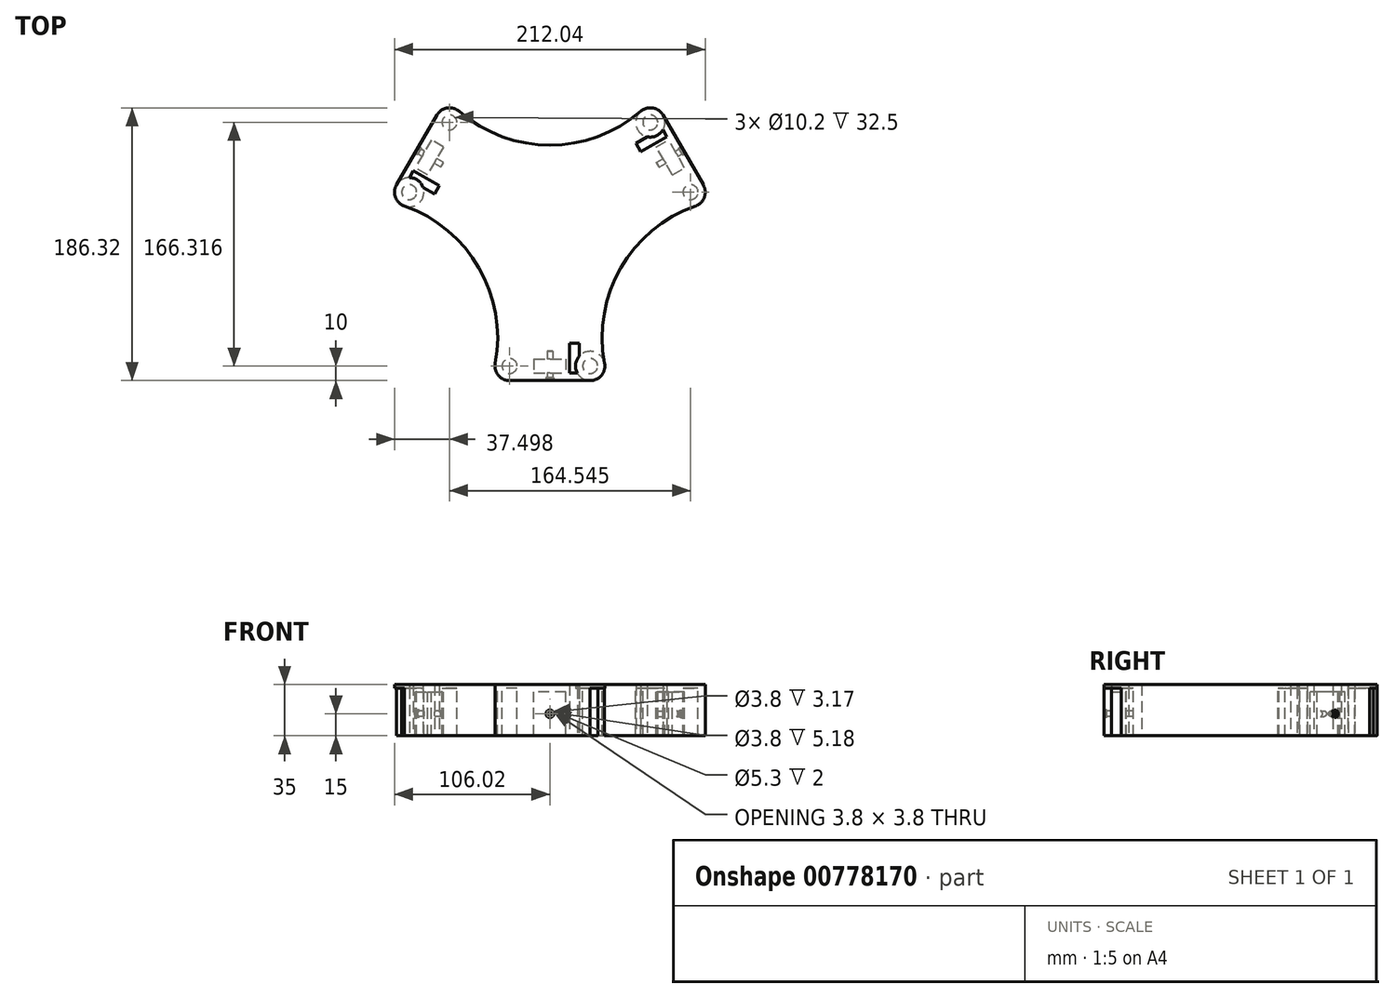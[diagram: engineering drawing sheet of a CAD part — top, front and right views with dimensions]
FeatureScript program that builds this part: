
annotation { "Feature Type Name" : "Feature", "Feature Type Description" : "" }
export const myFeature = defineFeature(function(context is Context, id is Id, definition is map)
    precondition{}
    {
        {
            var Q0;
            Q0=qCreatedBy(makeId("Top.planeOp"),FACE);
            var sketch = newSketch(context, id + "F0", { "sketchPlane" : qUnion([Q0])});
            skCircle(sketch, "E0", {"center": v(0, 0) * mm, "radius": 57.15 * mm, "construction": true});
            skLineSegment(sketch, "E1.bottom", {"start": v(110, 110) * mm, "end": v(-110, 110) * mm, "construction": true});
            skLineSegment(sketch, "E1.top", {"start": v(110, -110) * mm, "end": v(-110, -110) * mm, "construction": true});
            skLineSegment(sketch, "E1.left", {"start": v(110, 110) * mm, "end": v(110, -110) * mm, "construction": true});
            skLineSegment(sketch, "E1.right", {"start": v(-110, 110) * mm, "end": v(-110, -110) * mm, "construction": true});
            skLineSegment(sketch, "E2", {"start": v(0, 0) * mm, "end": v(0, -95) * mm});
            skLineSegment(sketch, "E3", {"start": v(0, 0) * mm, "end": v(-59.96, -34.62) * mm});
            skLineSegment(sketch, "E4", {"start": v(0, 0) * mm, "end": v(-61.29, 35.38) * mm});
            skLineSegment(sketch, "E5.MirrorCS", {"start": v(0, 0) * mm, "end": v(59.96, -34.62) * mm});
            skLineSegment(sketch, "E6.MirrorCS", {"start": v(0, 0) * mm, "end": v(61.29, 35.38) * mm});
            skCircle(sketch, "E7", {"center": v(-27.5, -95) * mm, "radius": 5.1 * mm});
            skCircle(sketch, "E8", {"center": v(-27.5, -95) * mm, "radius": 10 * mm});
            skCircle(sketch, "E9.MirrorC", {"center": v(27.5, -95) * mm, "radius": 10 * mm});
            skCircle(sketch, "E10.MirrorC", {"center": v(27.5, -95) * mm, "radius": 5.1 * mm});
            skLineSegment(sketch, "E11", {"start": v(-27.5, -105) * mm, "end": v(27.5, -105) * mm});
            skCircle(sketch, "E12.1.0", {"center": v(96.02, 23.68) * mm, "radius": 5.1 * mm});
            skCircle(sketch, "E12.1.1", {"center": v(96.02, 23.68) * mm, "radius": 10 * mm});
            skLineSegment(sketch, "E12.1.2", {"start": v(104.68, 28.68) * mm, "end": v(77.18, 76.32) * mm});
            skCircle(sketch, "E12.1.3", {"center": v(68.52, 71.32) * mm, "radius": 10 * mm});
            skCircle(sketch, "E12.1.4", {"center": v(68.52, 71.32) * mm, "radius": 5.1 * mm});
            skCircle(sketch, "E12.2.0", {"center": v(-68.52, 71.32) * mm, "radius": 5.1 * mm});
            skCircle(sketch, "E12.2.1", {"center": v(-68.52, 71.32) * mm, "radius": 10 * mm});
            skLineSegment(sketch, "E12.2.2", {"start": v(-77.18, 76.32) * mm, "end": v(-104.68, 28.68) * mm});
            skCircle(sketch, "E12.2.3", {"center": v(-96.02, 23.68) * mm, "radius": 10 * mm});
            skCircle(sketch, "E12.2.4", {"center": v(-96.02, 23.68) * mm, "radius": 5.1 * mm});
            skArc(sketch, "E13", {"start": v(99.32, 14.24) * mm, "mid": v(48.39, -27.94) * mm, "end": v(37.32, -93.14) * mm});
            skArc(sketch, "E14.1.0", {"start": v(-62, 78.9) * mm, "mid": v(0, 55.87) * mm, "end": v(62, 78.9) * mm});
            skArc(sketch, "E14.2.0", {"start": v(-37.32, -93.14) * mm, "mid": v(-48.39, -27.94) * mm, "end": v(-99.32, 14.24) * mm});
            skSolve(sketch);
        }
        {
            var Q0;
            {var subQ0=sQuery(id+"F0.wireOp",EDGE,"E11");Q0=makeQuery(id+"F0.imprint","IMPRINT",FACE,{"disambiguationData":[TD([[makeQuery(id+"F0.imprint","IMPRINT",EDGE,{"derivedFrom":subQ0}),1.0]])]});}
            var Q1;
            Q1=makeQuery(id+"F0.imprint","IMPRINT",FACE,{"disambiguationData":[TD([[makeQuery(id+"F0.imprint","IMPRINT",EDGE,{"derivedFrom":sQuery(id+"F0.wireOp",EDGE,"E7")}),-1.0]])]});
            var Q2;
            Q2=makeQuery(id+"F0.imprint","IMPRINT",FACE,{"disambiguationData":[TD([[makeQuery(id+"F0.imprint","IMPRINT",EDGE,{"derivedFrom":sQuery(id+"F0.wireOp",EDGE,"E10.MirrorC")}),1.0]])]});
            extrude(context, id + "F1", {"entities" : qUnion([Q0, Q1, Q2]), "oppositeDirection" : true, "depth" : 35 * mm, "offsetDistance" : 25 * mm});
        }
        {
            var Q0;
            Q0=makeQuery(id+"F1.opExtrude","CAP_FACE",FACE,{"disambiguationData":[OSD([sQuery(id+"F0.wireOp",EDGE,"E3"),sQuery(id+"F0.wireOp",EDGE,"E5.MirrorCS"),sQuery(id+"F0.wireOp",EDGE,"E7"),sQuery(id+"F0.wireOp",EDGE,"E8"),sQuery(id+"F0.wireOp",EDGE,"E9.MirrorC"),sQuery(id+"F0.wireOp",EDGE,"E10.MirrorC"),sQuery(id+"F0.wireOp",EDGE,"E11"),sQuery(id+"F0.wireOp",EDGE,"E13"),sQuery(id+"F0.wireOp",EDGE,"E14.2.0")])],"isStart":true});
            var sketch = newSketch(context, id + "F2", { "sketchPlane" : qUnion([Q0])});
            skLineSegment(sketch, "E15.0", {"start": v(-27.5, -105) * mm, "end": v(27.5, -105) * mm});
            skLineSegment(sketch, "E16.bottom", {"start": v(11, -99.83) * mm, "end": v(-11, -99.83) * mm});
            skLineSegment(sketch, "E16.top", {"start": v(11, -90.18) * mm, "end": v(-11, -90.18) * mm});
            skLineSegment(sketch, "E16.left", {"start": v(11, -99.83) * mm, "end": v(11, -90.18) * mm});
            skLineSegment(sketch, "E16.right", {"start": v(-11, -99.83) * mm, "end": v(-11, -90.18) * mm});
            skPoint(sketch, "E16.middle", {"position": v(0, -95) * mm});
            skPoint(sketch, "E16.middle.positionSnap0", {"position": v(0, -105) * mm});
            skPoint(sketch, "E16.centerSnap0", {"position": v(0, -105) * mm});
            skSolve(sketch);
        }
        {
            var Q0;
            Q0=makeQuery(id+"F2.imprint","IMPRINT",FACE,{"disambiguationData":[TD([[makeQuery(id+"F2.imprint","IMPRINT",EDGE,{"derivedFrom":sQuery(id+"F2.wireOp",EDGE,"E16.bottom")}),-1.0]])]});
            var Q1;
            Q1=makeQuery(id+"F1.opExtrude","CAP_FACE",FACE,{"disambiguationData":[OSD([sQuery(id+"F0.wireOp",EDGE,"E3"),sQuery(id+"F0.wireOp",EDGE,"E5.MirrorCS"),sQuery(id+"F0.wireOp",EDGE,"E7"),sQuery(id+"F0.wireOp",EDGE,"E8"),sQuery(id+"F0.wireOp",EDGE,"E9.MirrorC"),sQuery(id+"F0.wireOp",EDGE,"E10.MirrorC"),sQuery(id+"F0.wireOp",EDGE,"E11"),sQuery(id+"F0.wireOp",EDGE,"E13"),sQuery(id+"F0.wireOp",EDGE,"E14.2.0")])],"isStart":false});
            extrude(context, id + "F3", {"entities" : qUnion([Q0]), "operationType" : NewBodyOperationType.REMOVE, "endBound" : BoundingType.UP_TO_SURFACE, "oppositeDirection" : true, "depth" : 25 * mm, "endBoundEntityFace" : qUnion([Q1]), "offsetDistance" : 25 * mm});
        }
        {
            var Q0;
            Q0=makeQuery(id+"F2.imprint","IMPRINT",FACE,{"disambiguationData":[TD([[makeQuery(id+"F2.imprint","IMPRINT",EDGE,{"derivedFrom":sQuery(id+"F2.wireOp",EDGE,"E16.bottom")}),-1.0]])]});
            extrude(context, id + "F4", {"entities" : qUnion([Q0]), "operationType" : NewBodyOperationType.ADD, "oppositeDirection" : true, "depth" : 5 * mm, "offsetDistance" : 25 * mm});
        }
        {
            var Q0;
            Q0=makeQuery(id+"F0.imprint","IMPRINT",FACE,{"disambiguationData":[TD([[makeQuery(id+"F0.imprint","IMPRINT",EDGE,{"derivedFrom":sQuery(id+"F0.wireOp",EDGE,"E7")}),1.0]])]});
            var Q1;
            Q1=makeQuery(id+"F0.imprint","IMPRINT",FACE,{"disambiguationData":[TD([[makeQuery(id+"F0.imprint","IMPRINT",EDGE,{"derivedFrom":sQuery(id+"F0.wireOp",EDGE,"E10.MirrorC")}),-1.0]])]});
            extrude(context, id + "F5", {"entities" : qUnion([Q0, Q1]), "operationType" : NewBodyOperationType.ADD, "oppositeDirection" : true, "depth" : 2.5 * mm, "offsetDistance" : 25 * mm});
        }
        {
            var Q0;
            Q0=makeQuery(id+"F1.opExtrude","SWEPT_FACE",FACE,{"disambiguationData":[OSD([sQuery(id+"F0.wireOp",EDGE,"E11")])]});
            var sketch = newSketch(context, id + "F6", { "sketchPlane" : qUnion([Q0])});
            skLineSegment(sketch, "E17.0", {"start": v(-27.5, 0) * mm, "end": v(27.5, 0) * mm});
            skLineSegment(sketch, "E18.0", {"start": v(-27.5, -35) * mm, "end": v(27.5, -35) * mm});
            skLineSegment(sketch, "E19", {"start": v(0, 0) * mm, "end": v(0, -35) * mm, "construction": true});
            skPoint(sketch, "E20", {"position": v(0, -17.5) * mm});
            skCircle(sketch, "E21", {"center": v(0, -20) * mm, "radius": 4.15 * mm});
            skCircle(sketch, "E22", {"center": v(0, -20) * mm, "radius": 2.65 * mm});
            skCircle(sketch, "E23", {"center": v(0, -20) * mm, "radius": 1.9 * mm});
            skSolve(sketch);
        }
        {
            var Q0;
            Q0=makeQuery(id+"F6.imprint","IMPRINT",FACE,{"disambiguationData":[TD([[makeQuery(id+"F6.imprint","IMPRINT",EDGE,{"derivedFrom":sQuery(id+"F6.wireOp",EDGE,"E23")}),1.0]])]});
            extrude(context, id + "F7", {"entities" : qUnion([Q0]), "operationType" : NewBodyOperationType.REMOVE, "oppositeDirection" : true, "depth" : 20 * mm, "offsetDistance" : 25 * mm});
        }
        {
            var Q0;
            Q0=makeQuery(id+"F6.imprint","IMPRINT",FACE,{"disambiguationData":[TD([[makeQuery(id+"F6.imprint","IMPRINT",EDGE,{"derivedFrom":sQuery(id+"F6.wireOp",EDGE,"E22")}),1.0]])]});
            extrude(context, id + "F8", {"entities" : qUnion([Q0]), "operationType" : NewBodyOperationType.REMOVE, "oppositeDirection" : true, "depth" : 2 * mm, "offsetDistance" : 25 * mm});
        }
        {
            var Q0;
            Q0=makeQuery(id+"F1.opExtrude","CAP_FACE",FACE,{"disambiguationData":[OSD([sQuery(id+"F0.wireOp",EDGE,"E3"),sQuery(id+"F0.wireOp",EDGE,"E5.MirrorCS"),sQuery(id+"F0.wireOp",EDGE,"E7"),sQuery(id+"F0.wireOp",EDGE,"E8"),sQuery(id+"F0.wireOp",EDGE,"E9.MirrorC"),sQuery(id+"F0.wireOp",EDGE,"E10.MirrorC"),sQuery(id+"F0.wireOp",EDGE,"E11"),sQuery(id+"F0.wireOp",EDGE,"E13"),sQuery(id+"F0.wireOp",EDGE,"E14.2.0")])],"isStart":false});
            var sketch = newSketch(context, id + "F9", { "sketchPlane" : qUnion([Q0])});
            skLineSegment(sketch, "E24.bottom", {"start": v(20.02, 79.43) * mm, "end": v(13.37, 79.43) * mm});
            skLineSegment(sketch, "E24.top", {"start": v(20.02, 99.83) * mm, "end": v(13.37, 99.83) * mm});
            skLineSegment(sketch, "E24.left", {"start": v(20.02, 79.43) * mm, "end": v(20.02, 99.83) * mm});
            skLineSegment(sketch, "E24.right", {"start": v(13.37, 79.43) * mm, "end": v(13.37, 99.83) * mm});
            skPoint(sketch, "E24.middle", {"position": v(16.7, 89.63) * mm});
            skLineSegment(sketch, "E25.0", {"start": v(11, 99.83) * mm, "end": v(11, 90.18) * mm});
            skCircle(sketch, "E26.0", {"center": v(27.5, 95) * mm, "radius": 5.1 * mm});
            skLineSegment(sketch, "E27", {"start": v(11, 95) * mm, "end": v(13.37, 95) * mm});
            skLineSegment(sketch, "E28", {"start": v(22.4, 95) * mm, "end": v(20.02, 95) * mm});
            skSolve(sketch);
        }
        {
            var Q0;
            {var subQ3=sQuery(id+"F9.wireOp",EDGE,"E24.bottom");Q0=makeQuery(id+"F9.imprint","IMPRINT",FACE,{"disambiguationData":[TD([[makeQuery(id+"F9.imprint","IMPRINT",EDGE,{"derivedFrom":subQ3}),-1.0]])]});}
            var Q1;
            {var subQ0=sQuery(id+"F0.wireOp",EDGE,"E10.MirrorC");var subQ1=sQuery(id+"F0.wireOp",EDGE,"E7");Q1=makeQuery(id+"F5.boolean.opBoolean","MERGE",FACE,{"derivedFrom":[makeQuery(id+"F4.boolean.opBoolean","MERGE",FACE,{"derivedFrom":[makeQuery(id+"F1.opExtrude","CAP_FACE",FACE,{"disambiguationData":[OSD([sQuery(id+"F0.wireOp",EDGE,"E3"),sQuery(id+"F0.wireOp",EDGE,"E5.MirrorCS"),subQ1,sQuery(id+"F0.wireOp",EDGE,"E8"),sQuery(id+"F0.wireOp",EDGE,"E9.MirrorC"),subQ0,sQuery(id+"F0.wireOp",EDGE,"E11"),sQuery(id+"F0.wireOp",EDGE,"E13"),sQuery(id+"F0.wireOp",EDGE,"E14.2.0")])],"isStart":true}),makeQuery(id+"F4.opExtrude","CAP_FACE",FACE,{"disambiguationData":[OSD([sQuery(id+"F2.wireOp",EDGE,"E16.bottom"),sQuery(id+"F2.wireOp",EDGE,"E16.top"),sQuery(id+"F2.wireOp",EDGE,"E16.left"),sQuery(id+"F2.wireOp",EDGE,"E16.right")])],"isStart":true})]}),makeQuery(id+"F5.opExtrude","CAP_FACE",FACE,{"disambiguationData":[OSD([subQ1])],"isStart":true}),makeQuery(id+"F5.opExtrude","CAP_FACE",FACE,{"disambiguationData":[OSD([subQ0])],"isStart":true})]});}
            extrude(context, id + "F10", {"entities" : qUnion([Q0]), "operationType" : NewBodyOperationType.REMOVE, "endBound" : BoundingType.UP_TO_SURFACE, "oppositeDirection" : true, "depth" : 25 * mm, "endBoundEntityFace" : qUnion([Q1]), "offsetDistance" : 25 * mm});
        }
        {
            var Q0;
            Q0=makeQuery(id+"F1.opExtrude","SWEPT_BODY",BODY,{"disambiguationData":[OSD([sQuery(id+"F0.wireOp",EDGE,"E3"),sQuery(id+"F0.wireOp",EDGE,"E5.MirrorCS"),sQuery(id+"F0.wireOp",EDGE,"E7"),sQuery(id+"F0.wireOp",EDGE,"E8"),sQuery(id+"F0.wireOp",EDGE,"E9.MirrorC"),sQuery(id+"F0.wireOp",EDGE,"E10.MirrorC"),sQuery(id+"F0.wireOp",EDGE,"E11"),sQuery(id+"F0.wireOp",EDGE,"E13"),sQuery(id+"F0.wireOp",EDGE,"E14.2.0")])]});
            var Q1;
            Q1=sQuery(id+"F0.wireOp",EDGE,"E0");
            circularPattern(context, id + "F11", {"operationType" : NewBodyOperationType.ADD, "entities" : qUnion([Q0]), "axis" : qUnion([Q1]), "angle" : 240 * degree, "instanceCount" : 3, "equalSpace" : true});
        }
    });
